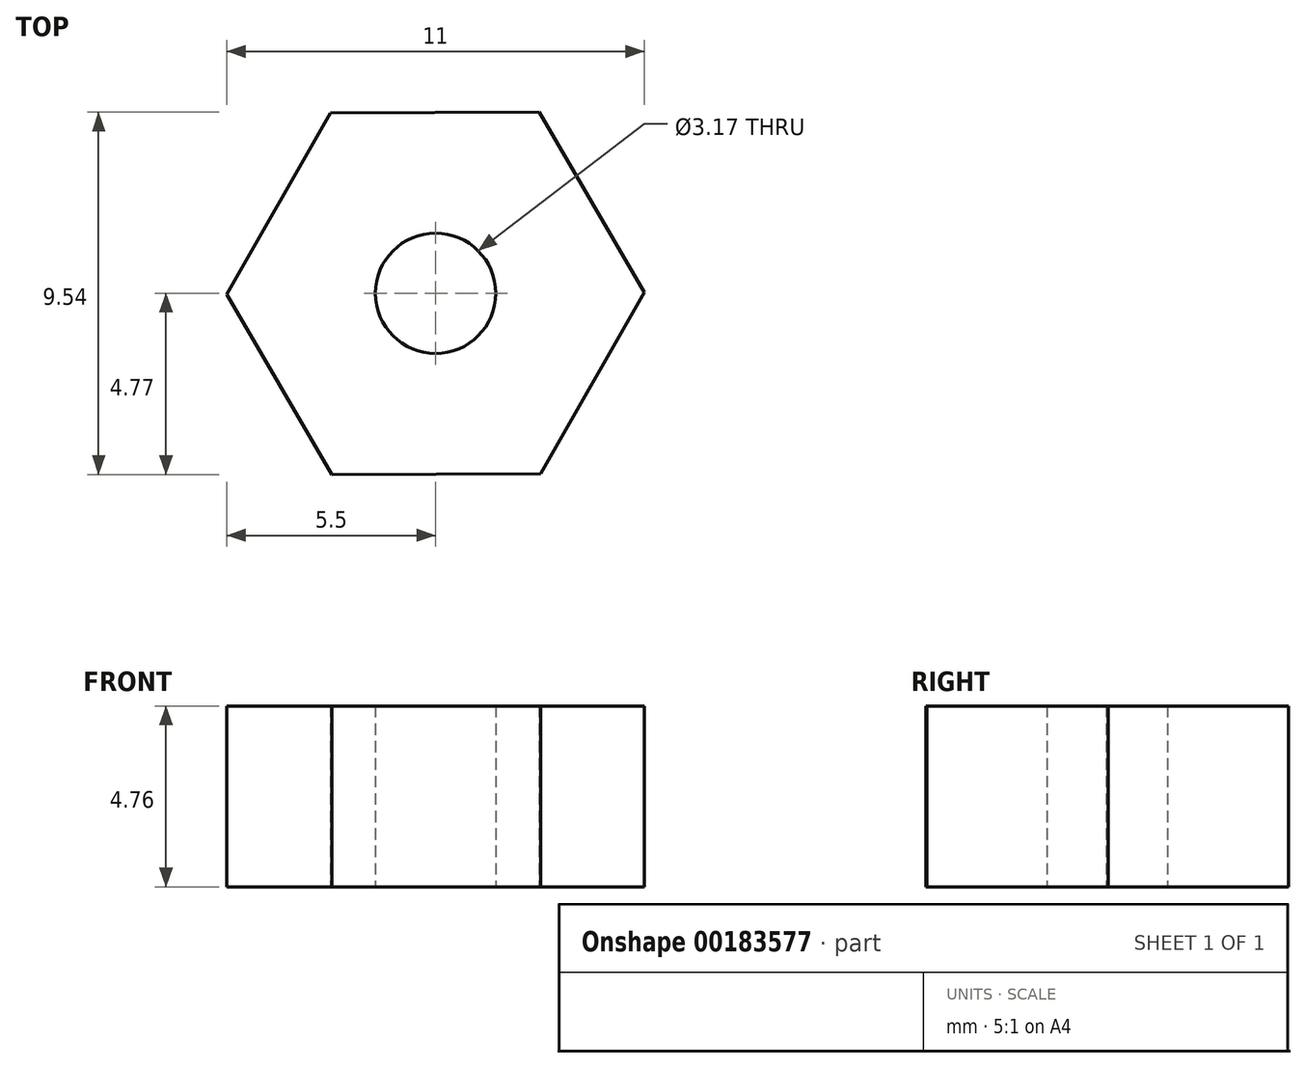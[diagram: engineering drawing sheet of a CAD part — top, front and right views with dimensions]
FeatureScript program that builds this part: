
annotation { "Feature Type Name" : "Feature", "Feature Type Description" : "" }
export const myFeature = defineFeature(function(context is Context, id is Id, definition is map)
    precondition{}
    {
        {
            var Q0;
            Q0=qCreatedBy(makeId("Top.planeOp"),FACE);
            var sketch = newSketch(context, id + "F0", { "sketchPlane" : qUnion([Q0])});
            skCircle(sketch, "E0.cCircle", {"center": v(0, 0) * mm, "radius": 4.76 * mm, "construction": true});
            skLineSegment(sketch, "E0.0", {"start": v(2.73, 4.77) * mm, "end": v(5.5, 0.02) * mm});
            skLineSegment(sketch, "E0.1", {"start": v(5.5, 0.02) * mm, "end": v(2.77, -4.75) * mm});
            skLineSegment(sketch, "E0.2", {"start": v(2.77, -4.75) * mm, "end": v(-2.73, -4.77) * mm});
            skLineSegment(sketch, "E0.3", {"start": v(-2.73, -4.77) * mm, "end": v(-5.5, -0.02) * mm});
            skLineSegment(sketch, "E0.4", {"start": v(-5.5, -0.02) * mm, "end": v(-2.77, 4.75) * mm});
            skLineSegment(sketch, "E0.5", {"start": v(-2.77, 4.75) * mm, "end": v(2.73, 4.77) * mm});
            skPoint(sketch, "E0.0.midPoint", {"position": v(4.11, 2.4) * mm});
            skCircle(sketch, "E1", {"center": v(0, 0) * mm, "radius": 1.58 * mm});
            skSolve(sketch);
        }
        {
            var Q0;
            Q0 = qSketchRegion(id + "F0", true);
            extrude(context, id + "F1", {"entities" : qUnion([Q0]), "depth" : 4.76 * mm});
        }
    });
